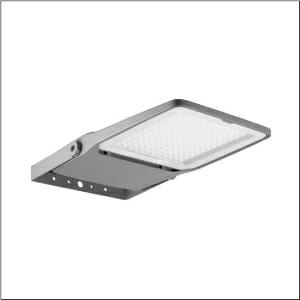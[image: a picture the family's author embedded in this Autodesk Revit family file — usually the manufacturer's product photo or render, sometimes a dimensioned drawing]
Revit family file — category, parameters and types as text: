
# Revit family: floodlight_fl_20_midi___rs05_5xa7682g2h2ac_5173
name_source: partatom
category: Lighting Fixtures
units: mm (PartAtom-declared; Revit-internal decimal feet)

## family parameters
Cut with Voids When Loaded = No
Host = Face
Light Source = No
Part Type = Normal
Room Calculation Point = No
Round Connector Dimension = Use Diameter
Shared = No

## types (1)
- --- (1 x LED 4000K / CRI = 70 (unbekannt), 38380 lm, 4000K)
    Apparent Load = 306 VA
    CIE Flux Codes = 81 94 99 100 100
    Color Rendering = 70
    Color Temperature = 4000K
    Default Elevation = 1800 mm
    Description = Floodlight FL 20 midi, floodlight, primary light control with lens, of plastic, primary optical cover: protective disc, of toughened safety glass, transparent, light distribution: RS05, light emission: direct distribution, primary light characteristic: rotationally symmetric, installation type: surface-mounted, LED, High Power LED, rated luminous flux: 38.380lm, luminous efficacy: 126lm/W, light colour: 740, colour temperature: 4000K, control gear: ECG Plus, control: overheat protection, power reduction, digital communication interface, time-dependent luminous flux control, flexible luminous flux parameterisation, electronic power reduction, with terminal, 10-pole, max. 2.5mm², mains connection: 220..240V, AC, 50/60Hz, rated input power: 306W, LED unit, of diecast aluminium, powder-coated, Siteco® metallic grey (DB 702S), corrosivity category C5 mid according to DIN EN ISO 12944, length: 731mm, width: 450mm, height: 76mm, housing frame, of diecast aluminium, powder-coated, Siteco® metallic grey (DB 702S), wall fastening, DALI, protection rating (complete): IP66, insulation class (complete): insulation class II (safety insulation), certification: CE, ENEC, VDE, protection symbol: D, permissible operating ambient temperature: -40..+40°C, permissible operating ambient temperature for outdoor applications: -40..+50°C, standard: DIN EN 12944, packaging unit: 1 piece

Light Distribution: RS05
    Height = 76 mm
    Lamp = 1 x LED 4000K / CRI >= 70 (unbekannt)
    Lamp Light Flux = 38380 lm
    Lamp count = 1
    Length = 731 mm
    Luminous efficacy = 126 lm/W
    Manufacturer = Siteco
    ModVariant = No
    Model = 5XA7682G2H2AC
    Number of Poles = 1
    OnlyDefault = Yes
    Power Factor = 1
    Product Name = Floodlight FL 20 midi | RS05
    Product group = floodlight | pylon annexe
    ProductGroupID = 6200
    Protection Class = Protection class II
    Protection Degree = IP 66
    RLX_Detail_Level = 1
    RLX_Emergency_Light_Flux = 0 lm
    RLX_Emergency_Type = 0
    RLX_Emergency_Type_DB = No
    RlxData = <blob elided: 86597 chars, md5=aa605258>
    Socket = socket
    Standby Power = 0 W
    System Light Flux = 38380 lm
    System Power = 306 W
    Type Comments = factory setting: luminous flux: 100 % | dim-lin: 254 | 700 mA
    Type Image = l_1005944.jpg
    URL = http://relux.com
    VarID = @adj_146305
    Voltage = 0 V
    Weight = 0.00 kg
    Width = 450 mm

## geometry (parser evidence)
native form markers: Blend x4, Sweep x13
no freeform markers — native parametric forms only
